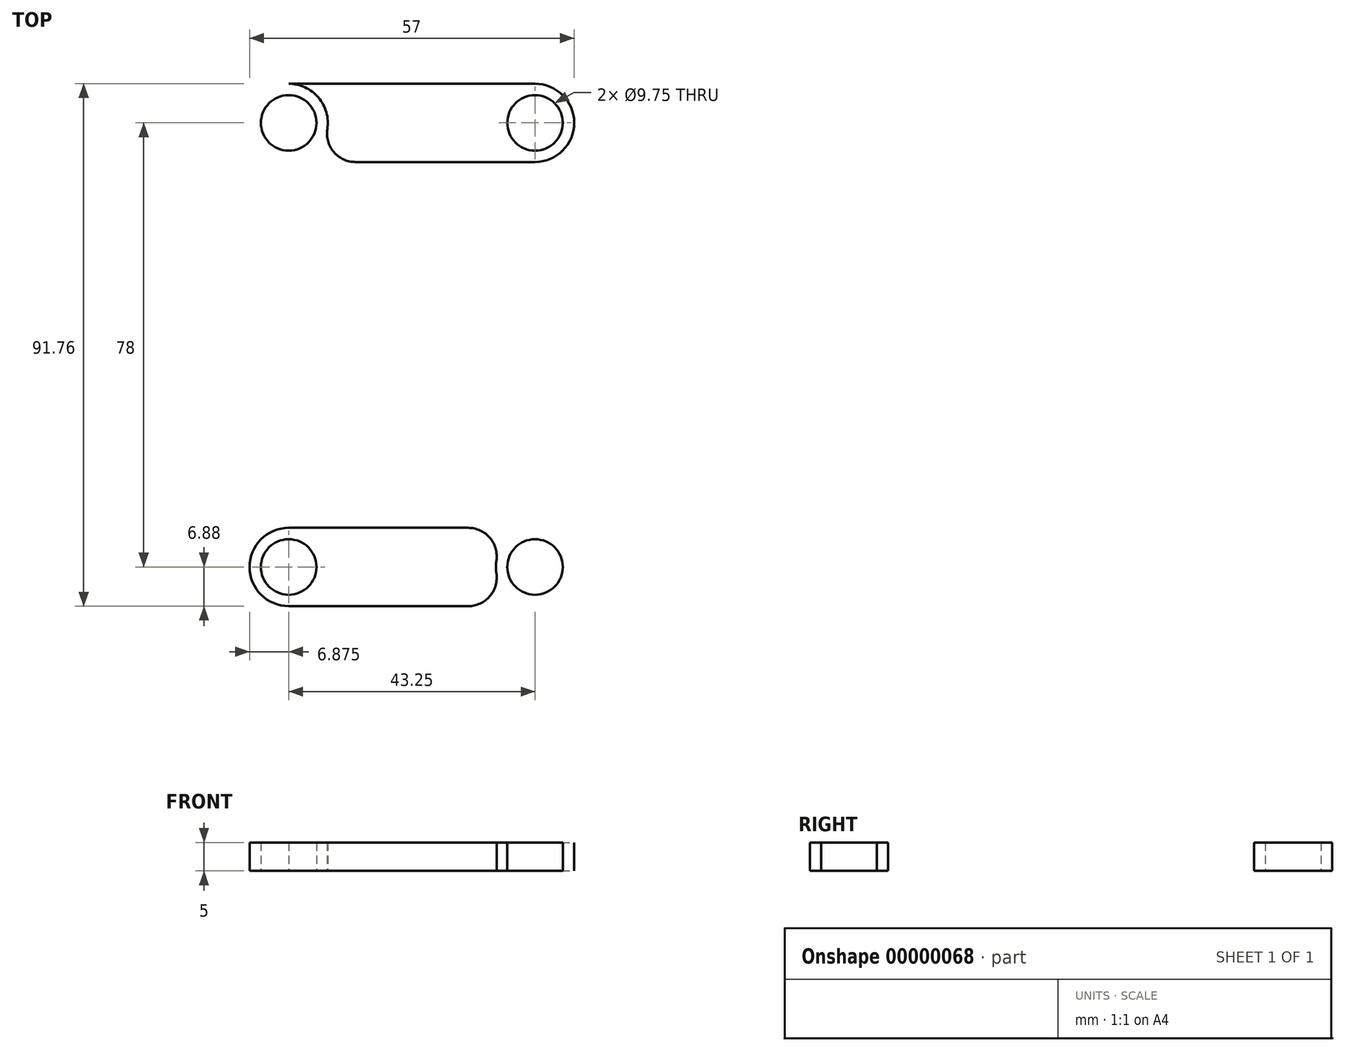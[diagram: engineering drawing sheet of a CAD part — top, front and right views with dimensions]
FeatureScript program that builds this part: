
annotation { "Feature Type Name" : "Feature", "Feature Type Description" : "" }
export const myFeature = defineFeature(function(context is Context, id is Id, definition is map)
    precondition{}
    {
        {
            var Q0;
            Q0=qCreatedBy(makeId("Top.planeOp"),FACE);
            var sketch = newSketch(context, id + "F0", { "sketchPlane" : qUnion([Q0])});
            skCircle(sketch, "E0", {"center": v(-21.62, 0) * mm, "radius": 4.88 * mm});
            skLineSegment(sketch, "E1", {"start": v(0, 0) * mm, "end": v(0, 41.28) * mm, "construction": true});
            skCircle(sketch, "E2", {"center": v(-21.62, 0) * mm, "radius": 6.87 * mm});
            skLineSegment(sketch, "E3", {"start": v(0, 0) * mm, "end": v(-14.75, 0) * mm, "construction": true});
            skLineSegment(sketch, "E4", {"start": v(0, 39) * mm, "end": v(-36.27, 39) * mm, "construction": true});
            skCircle(sketch, "E5.MirrorC", {"center": v(-21.62, 78) * mm, "radius": 4.88 * mm});
            skCircle(sketch, "E6.MirrorC", {"center": v(-21.62, 78) * mm, "radius": 6.87 * mm});
            skCircle(sketch, "E7.MirrorC", {"center": v(21.62, 78) * mm, "radius": 6.87 * mm});
            skCircle(sketch, "E8.MirrorC", {"center": v(21.62, 78) * mm, "radius": 4.88 * mm});
            skCircle(sketch, "E9.MirrorC", {"center": v(21.62, 0) * mm, "radius": 4.88 * mm});
            skCircle(sketch, "E10.MirrorC", {"center": v(21.62, 0) * mm, "radius": 6.87 * mm});
            skLineSegment(sketch, "E11", {"start": v(-21.62, 84.88) * mm, "end": v(21.62, 84.88) * mm});
            skLineSegment(sketch, "E12", {"start": v(-21.62, 71.12) * mm, "end": v(21.62, 71.12) * mm});
            skLineSegment(sketch, "E13.bottom", {"start": v(-5, 71.12) * mm, "end": v(5, 71.12) * mm});
            skLineSegment(sketch, "E13.top", {"start": v(-5, 6.88) * mm, "end": v(5, 6.88) * mm});
            skLineSegment(sketch, "E13.left", {"start": v(-5, 71.12) * mm, "end": v(-5, 6.88) * mm});
            skLineSegment(sketch, "E13.right", {"start": v(5, 71.12) * mm, "end": v(5, 6.88) * mm});
            skPoint(sketch, "E13.middle", {"position": v(0, 39) * mm});
            skLineSegment(sketch, "E14", {"start": v(-21.62, 6.88) * mm, "end": v(-5, 6.88) * mm});
            skLineSegment(sketch, "E15.MirrorCS", {"start": v(21.62, 6.88) * mm, "end": v(5, 6.88) * mm});
            skLineSegment(sketch, "E16.MirrorCS", {"start": v(-5, -71.12) * mm, "end": v(5, -71.12) * mm});
            skLineSegment(sketch, "E17.MirrorCS", {"start": v(-5, -71.12) * mm, "end": v(-5, -6.88) * mm});
            skPoint(sketch, "E18.MirrorP", {"position": v(0, -39) * mm});
            skLineSegment(sketch, "E19.MirrorCS", {"start": v(-5, -6.88) * mm, "end": v(5, -6.88) * mm});
            skLineSegment(sketch, "E20.MirrorCS", {"start": v(5, -71.12) * mm, "end": v(5, -6.88) * mm});
            skLineSegment(sketch, "E21.MirrorCS", {"start": v(-21.62, -6.87) * mm, "end": v(-5, -6.88) * mm});
            skCircle(sketch, "E22.MirrorC", {"center": v(-21.63, -78) * mm, "radius": 4.88 * mm});
            skLineSegment(sketch, "E23.MirrorCS", {"start": v(-21.62, -84.88) * mm, "end": v(21.63, -84.88) * mm});
            skLineSegment(sketch, "E24.MirrorCS", {"start": v(-21.62, -71.12) * mm, "end": v(21.63, -71.12) * mm});
            skCircle(sketch, "E25.MirrorC", {"center": v(-21.63, -78) * mm, "radius": 6.87 * mm});
            skCircle(sketch, "E26.MirrorC", {"center": v(21.63, -78) * mm, "radius": 6.87 * mm});
            skLineSegment(sketch, "E27.MirrorCS", {"start": v(21.62, -6.87) * mm, "end": v(5, -6.88) * mm});
            skCircle(sketch, "E28.MirrorC", {"center": v(21.63, -78) * mm, "radius": 4.88 * mm});
            skSolve(sketch);
        }
        {
            var Q0;
            Q0=makeQuery(id+"F0.imprint","IMPRINT",FACE,{"disambiguationData":[TD([[makeQuery(id+"F0.imprint","IMPRINT",EDGE,{"derivedFrom":sQuery(id+"F0.wireOp",EDGE,"E0")}),-1.0]])]});
            var Q1;
            Q1=makeQuery(id+"F0.imprint","IMPRINT",FACE,{"disambiguationData":[TD([[makeQuery(id+"F0.imprint","IMPRINT",EDGE,{"derivedFrom":sQuery(id+"F0.wireOp",EDGE,"E5.MirrorC")}),1.0]])]});
            var Q2;
            Q2=makeQuery(id+"F0.imprint","IMPRINT",FACE,{"disambiguationData":[TD([[makeQuery(id+"F0.imprint","IMPRINT",EDGE,{"derivedFrom":sQuery(id+"F0.wireOp",EDGE,"E8.MirrorC")}),-1.0]])]});
            var Q3;
            Q3=makeQuery(id+"F0.imprint","IMPRINT",FACE,{"disambiguationData":[TD([[makeQuery(id+"F0.imprint","IMPRINT",EDGE,{"derivedFrom":sQuery(id+"F0.wireOp",EDGE,"E9.MirrorC")}),1.0]])]});
            var Q4;
            Q4=makeQuery(id+"F0.imprint","IMPRINT",FACE,{"disambiguationData":[TD([[makeQuery(id+"F0.imprint","IMPRINT",EDGE,{"derivedFrom":sQuery(id+"F0.wireOp",EDGE,"E13.bottom")}),-1.0]])]});
            var Q5;
            {var subQ4=sQuery(id+"F0.wireOp",EDGE,"E11");Q5=makeQuery(id+"F0.imprint","IMPRINT",FACE,{"disambiguationData":[TD([[makeQuery(id+"F0.imprint","IMPRINT",EDGE,{"derivedFrom":subQ4}),-1.0]])]});}
            var Q6;
            Q6=makeQuery(id+"F0.imprint","IMPRINT",FACE,{"disambiguationData":[TD([[makeQuery(id+"F0.imprint","IMPRINT",EDGE,{"derivedFrom":sQuery(id+"F0.wireOp",EDGE,"E13.top")}),-1.0]])]});
            extrude(context, id + "F1", {"entities" : qUnion([Q0, Q1, Q2, Q3, Q4, Q5, Q6]), "depth" : 5 * mm});
        }
        {
            var Q0;
            Q0=makeQuery(id+"F1.opExtrude","SWEPT_EDGE",EDGE,{"disambiguationData":[OSD([sQuery(id+"F0.wireOp",EDGE,"E12"),sQuery(id+"F0.wireOp",EDGE,"E13.bottom"),sQuery(id+"F0.wireOp",EDGE,"E13.left")])]});
            var Q1;
            Q1=makeQuery(id+"F1.opExtrude","SWEPT_EDGE",EDGE,{"disambiguationData":[OSD([sQuery(id+"F0.wireOp",EDGE,"E12"),sQuery(id+"F0.wireOp",EDGE,"E13.bottom"),sQuery(id+"F0.wireOp",EDGE,"E13.right")])]});
            var Q2;
            Q2=makeQuery(id+"F1.opExtrude","SWEPT_EDGE",EDGE,{"disambiguationData":[OSD([sQuery(id+"F0.wireOp",EDGE,"E13.top"),sQuery(id+"F0.wireOp",EDGE,"E13.right"),sQuery(id+"F0.wireOp",EDGE,"E15.MirrorCS")])]});
            var Q3;
            Q3=makeQuery(id+"F1.opExtrude","SWEPT_EDGE",EDGE,{"disambiguationData":[OSD([sQuery(id+"F0.wireOp",EDGE,"E13.top"),sQuery(id+"F0.wireOp",EDGE,"E13.left"),sQuery(id+"F0.wireOp",EDGE,"E14")])]});
            var Q4;
            Q4=makeQuery(id+"F1.opExtrude","SWEPT_EDGE",EDGE,{"disambiguationData":[OSD([sQuery(id+"F0.wireOp",EDGE,"E17.MirrorCS"),sQuery(id+"F0.wireOp",EDGE,"E19.MirrorCS"),sQuery(id+"F0.wireOp",EDGE,"E21.MirrorCS")])]});
            var Q5;
            Q5=makeQuery(id+"F1.opExtrude","SWEPT_EDGE",EDGE,{"disambiguationData":[OSD([sQuery(id+"F0.wireOp",EDGE,"E19.MirrorCS"),sQuery(id+"F0.wireOp",EDGE,"E20.MirrorCS"),sQuery(id+"F0.wireOp",EDGE,"E27.MirrorCS")])]});
            var Q6;
            Q6=makeQuery(id+"F1.opExtrude","SWEPT_EDGE",EDGE,{"disambiguationData":[OSD([sQuery(id+"F0.wireOp",EDGE,"E20.MirrorCS"),sQuery(id+"F0.wireOp",EDGE,"E24.MirrorCS")])]});
            var Q7;
            Q7=makeQuery(id+"F1.opExtrude","SWEPT_EDGE",EDGE,{"disambiguationData":[OSD([sQuery(id+"F0.wireOp",EDGE,"E17.MirrorCS"),sQuery(id+"F0.wireOp",EDGE,"E24.MirrorCS")])]});
            fillet(context, id + "F2", {"entities" : qUnion([Q0, Q1, Q2, Q3, Q4, Q5, Q6, Q7]), "radius" : 5 * mm, "tangentPropagation" : true, "allowEdgeOverflow" : false});
        }
    });
